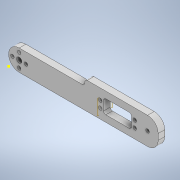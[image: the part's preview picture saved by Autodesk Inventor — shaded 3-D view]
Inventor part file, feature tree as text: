
AUTODESK INVENTOR PART (.ipt)
format: ipt  version: 2020 (Build 240168000, 168)  size: 291,328 bytes
history: native  units: in
note: dims shown in document units (in); Inventor stores cm internally (conversion verified against a paired STEP export)
features: sketch x14, extrude x9, fillet x5, plane x1
ambient origin geometry x8: Origin, YZ Plane, XZ Plane, XY Plane, X Axis, Y Axis, Z Axis, Center Point
bodies: Solid1 (feature_tree)
feature tree (29):
  sketch  "Sketch1"  dims[d0=8.5in d1=2.0in]
  extrude  "Extrusion1"  Depth=8.5in
  extrude  "Extrusion2"  Depth=1.2in
  extrude  "Extrusion3"  Depth=1.2in
  extrude  "Extrusion4"  Depth=1.0in
  extrude  "Extrusion6"  Depth=0.375in
  sketch  "Sketch8"  dims[d17=1.0in d18=0.0in d19=0.189in]
  sketch  "Sketch9"  dims[d20=0.173in d21=0.1772in d22=0.3898in d23=0.177in]
  sketch  "Sketch10"  dims[d24=0.189in d25=0.173in]
  fillet  "Fillet1"  Radius=1.6in
  fillet  "Fillet2"  Radius=1.5827in
  fillet  "Fillet3"  Radius=0.7874in
  extrude  "Extrusion7"  Depth=1.2in
  extrude  "Extrusion8"  Depth=0.189in
  sketch  "Sketch13"  dims[d28=0.177in]
  plane  "Work Plane1"
  sketch  "Sketch14"  dims[d29=1.0in d30=0.0in]
  extrude  "Extrusion9"  Depth=0.1772in
  fillet  "Fillet4"  Radius=0.3898in
  fillet  "Fillet5"  Radius=0.177in
  extrude  "Extrusion10"  Depth=0.173in
  sketch  "Sketch2"  dims[d2=0.375in d3=0.0in d4=1.2in]
  sketch  "Sketch3"  dims[d5=1.2in d6=0.5in]
  sketch  "Sketch4"  dims[d7=1.0in d8=1.0in]
  sketch  "Sketch5"  dims[d9=1.6in d10=0.375in d11=1.6in d12=1.5827in d13=0.7874in]
  sketch  "Sketch7"  dims[d14=1.0in d15=0.0in d16=1.2in]
  sketch  "Sketch11"  dims[d26=0.177in]
  sketch  "Sketch12"  dims[d27=0.39in]
  sketch  "Sketch15"  dims[d33=0.177in d34=1.0in d35=0.0in d36=0.125in d37=0.125in d38=0.6in d39=0.6in d40=0.3in d41=0.107in d42=0.107in d43=0.107in d44=0.107in d45=1.0in d46=0.0in d47=0.177in d48=0.177in d49=0.177in d50=0.177in d51=0.2in d52=0.2in d53=0.2in d54=0.2in d55=0.2in d56=0.2in d57=0.2in d58=0.2in d59=0.2in d60=1.0in d61=0.0in d62=0.375in d63=1.0in d64=0.0in d65=0.6in d66=0.125in d68=0.2in d69=1.0in d70=0.0in d31=0.5in d32=0.0344in]
